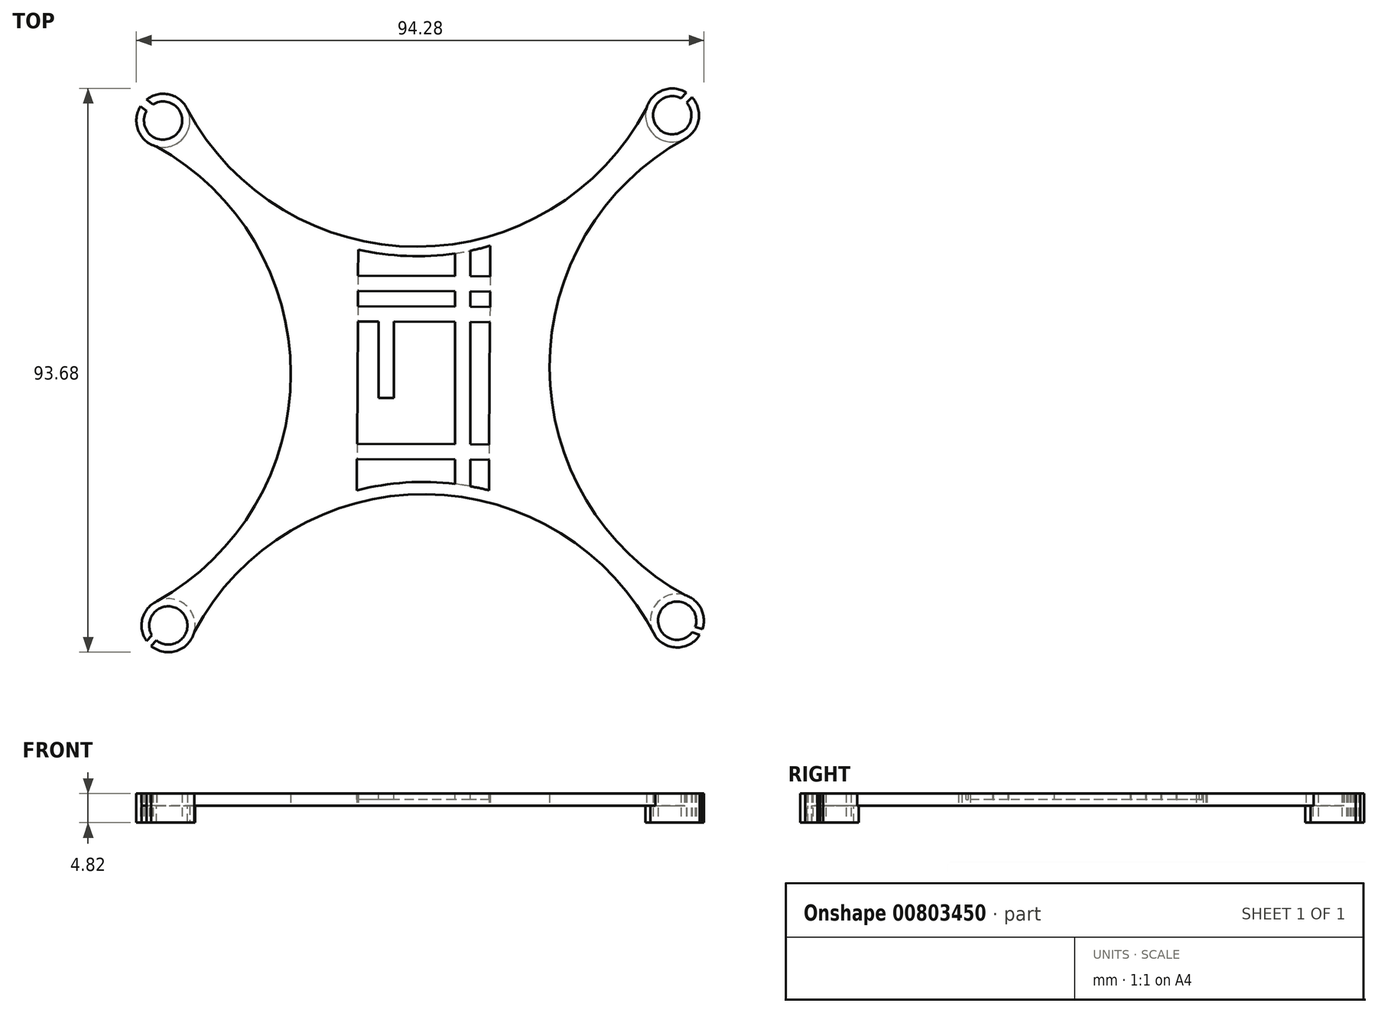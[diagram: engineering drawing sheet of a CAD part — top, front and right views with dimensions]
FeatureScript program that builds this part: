
annotation { "Feature Type Name" : "Feature", "Feature Type Description" : "" }
export const myFeature = defineFeature(function(context is Context, id is Id, definition is map)
    precondition{}
    {
        {
            var Q0;
            Q0=qCreatedBy(makeId("Top.planeOp"),FACE);
            var sketch = newSketch(context, id + "F0", { "sketchPlane" : qUnion([Q0])});
            skArc(sketch, "E0", {"start": v(2.55, 81.04) * mm, "mid": v(3.15, 81.98) * mm, "end": v(3.5, 83.03) * mm});
            skArc(sketch, "E1", {"start": v(3.18, 85.76) * mm, "mid": v(41.34, 62.94) * mm, "end": v(79.42, 85.92) * mm});
            skArc(sketch, "E2", {"start": v(-1.89, 4.02) * mm, "mid": v(20.35, 41.83) * mm, "end": v(-1.97, 79.6) * mm});
            skArc(sketch, "E3", {"start": v(80.92, 3.4) * mm, "mid": v(80.5, 2.69) * mm, "end": v(80.22, 1.92) * mm});
            skArc(sketch, "E4", {"start": v(80.89, -1.76) * mm, "mid": v(42.83, 21.8) * mm, "end": v(4.32, -1.04) * mm});
            skArc(sketch, "E5", {"start": v(85.7, 80.8) * mm, "mid": v(63.32, 42.87) * mm, "end": v(85.88, 5.03) * mm});
            skArc(sketch, "E6", {"start": v(81.15, 81.15) * mm, "mid": v(81.88, 80.73) * mm, "end": v(82.67, 80.46) * mm});
            skArc(sketch, "E7", {"start": v(3.94, 1.18) * mm, "mid": v(2.62, 3.23) * mm, "end": v(0.42, 4.27) * mm});
            skArc(sketch, "E8", {"start": v(0.73, 3.1) * mm, "mid": v(-2.56, 1.87) * mm, "end": v(-2.73, -1.63) * mm});
            skArc(sketch, "E9", {"start": v(81.97, 2.67) * mm, "mid": v(82.61, -1.74) * mm, "end": v(87.03, -1.15) * mm});
            skArc(sketch, "E10", {"start": v(82.1, 82.04) * mm, "mid": v(86.16, 82.75) * mm, "end": v(86.11, 86.86) * mm});
            skArc(sketch, "E11", {"start": v(1.5, 81.77) * mm, "mid": v(1.56, 85.95) * mm, "end": v(-2.56, 86.58) * mm});
            skArc(sketch, "E12", {"start": v(0.42, 4.27) * mm, "mid": v(22.13, 41.92) * mm, "end": v(0.7, 79.73) * mm});
            skArc(sketch, "E13", {"start": v(3.5, 83.03) * mm, "mid": v(41.63, 61.36) * mm, "end": v(79.42, 83.63) * mm});
            skArc(sketch, "E14", {"start": v(82.61, 80.55) * mm, "mid": v(61.39, 42.55) * mm, "end": v(83.44, 5.02) * mm});
            skArc(sketch, "E15", {"start": v(80.22, 1.92) * mm, "mid": v(41.87, 23.84) * mm, "end": v(3.94, 1.18) * mm});
            skArc(sketch, "E16.trimOffspring", {"start": v(79.42, 83.63) * mm, "mid": v(79.74, 82.8) * mm, "end": v(80.21, 82.04) * mm});
            skArc(sketch, "E17.trimOffspring", {"start": v(85.7, 80.8) * mm, "mid": v(88.09, 83.98) * mm, "end": v(86.99, 87.79) * mm});
            skLineSegment(sketch, "E18.left", {"start": v(31.55, 62.46) * mm, "end": v(31.32, 22.44) * mm});
            skLineSegment(sketch, "E18.right", {"start": v(53.5, 63.1) * mm, "end": v(53.27, 22.44) * mm});
            skLineSegment(sketch, "E19", {"start": v(-2.56, 86.58) * mm, "end": v(-3.62, 87.38) * mm});
            skLineSegment(sketch, "E20", {"start": v(-3.6, 85.5) * mm, "end": v(-4.61, 86.28) * mm});
            skArc(sketch, "E21.trimOffspring", {"start": v(-4.61, 86.28) * mm, "mid": v(-5, 82.26) * mm, "end": v(-1.97, 79.6) * mm});
            skArc(sketch, "E22.trimOffspring", {"start": v(-3.6, 85.5) * mm, "mid": v(-2.74, 81.34) * mm, "end": v(1.5, 81.77) * mm});
            skLineSegment(sketch, "E23", {"start": v(80.21, 82.04) * mm, "end": v(81.15, 81.15) * mm});
            skPoint(sketch, "E24.start.orphan", {"position": v(82.1, 82.04) * mm});
            skLineSegment(sketch, "E25", {"start": v(85.16, 87.6) * mm, "end": v(86.07, 88.55) * mm});
            skLineSegment(sketch, "E26", {"start": v(86.11, 86.86) * mm, "end": v(86.99, 87.79) * mm});
            skArc(sketch, "E27.trimOffspring", {"start": v(86.07, 88.55) * mm, "mid": v(82.08, 88.91) * mm, "end": v(79.42, 85.92) * mm});
            skArc(sketch, "E28.trimOffspring", {"start": v(85.16, 87.6) * mm, "mid": v(80.93, 86.31) * mm, "end": v(82.1, 82.04) * mm});
            skLineSegment(sketch, "E29", {"start": v(87.53, -0.22) * mm, "end": v(88.73, -0.65) * mm});
            skLineSegment(sketch, "E30", {"start": v(87.03, -1.15) * mm, "end": v(88.27, -1.6) * mm});
            skArc(sketch, "E31.trimOffspring", {"start": v(87.53, -0.22) * mm, "mid": v(85.99, 3.61) * mm, "end": v(81.97, 2.67) * mm});
            skArc(sketch, "E32.trimOffspring", {"start": v(88.73, -0.65) * mm, "mid": v(88.5, 2.8) * mm, "end": v(85.88, 5.03) * mm});
            skArc(sketch, "E33.trimOffspring", {"start": v(80.89, -1.76) * mm, "mid": v(84.62, -3.65) * mm, "end": v(88.27, -1.6) * mm});
            skArc(sketch, "E34.trimOffspring", {"start": v(83.49, 5.12) * mm, "mid": v(82.05, 4.49) * mm, "end": v(80.92, 3.4) * mm});
            skArc(sketch, "E35.trimOffspring", {"start": v(3.18, 85.76) * mm, "mid": v(0.17, 88.22) * mm, "end": v(-3.62, 87.38) * mm});
            skArc(sketch, "E36.trimOffspring", {"start": v(0.7, 79.73) * mm, "mid": v(1.7, 80.27) * mm, "end": v(2.55, 81.04) * mm});
            skArc(sketch, "E37.trimOffspring", {"start": v(-1.89, 4.02) * mm, "mid": v(-4.3, 1.13) * mm, "end": v(-3.63, -2.57) * mm});
            skLineSegment(sketch, "E38", {"start": v(-2.73, -1.63) * mm, "end": v(-3.63, -2.57) * mm});
            skLineSegment(sketch, "E39", {"start": v(-1.99, -2.48) * mm, "end": v(-2.87, -3.4) * mm});
            skArc(sketch, "E40.trimOffspring", {"start": v(-1.99, -2.48) * mm, "mid": v(2.85, -1.4) * mm, "end": v(0.73, 3.1) * mm});
            skArc(sketch, "E41.trimOffspring", {"start": v(-2.87, -3.4) * mm, "mid": v(1.39, -4.22) * mm, "end": v(4.32, -1.04) * mm});
            skSolve(sketch);
        }
        {
            var Q0;
            Q0 = qSketchRegion(id + "F0", true);
            var Q1;
            {var subQ1=sQuery(id+"F0.wireOp",EDGE,"E0");Q1=makeQuery(id+"F0.imprint","IMPRINT",FACE,{"disambiguationData":[TD([[makeQuery(id+"F0.imprint","IMPRINT",EDGE,{"derivedFrom":subQ1}),-1.0]])]});}
            var Q2;
            {var subQ10=sQuery(id+"F0.wireOp",EDGE,"E3");Q2=makeQuery(id+"F0.imprint","IMPRINT",FACE,{"disambiguationData":[TD([[makeQuery(id+"F0.imprint","IMPRINT",EDGE,{"derivedFrom":subQ10}),-1.0]])]});}
            extrude(context, id + "F1", {"entities" : qUnion([Q0, Q1, Q2]), "depth" : 2.03 * mm, "offsetDistance" : 25.4 * mm});
        }
        {
            var Q0;
            Q0=makeQuery(id+"F1.opExtrude","CAP_FACE",FACE,{"disambiguationData":[OSD([sQuery(id+"F0.wireOp",EDGE,"E1"),sQuery(id+"F0.wireOp",EDGE,"E2"),sQuery(id+"F0.wireOp",EDGE,"E4"),sQuery(id+"F0.wireOp",EDGE,"E5"),sQuery(id+"F0.wireOp",EDGE,"E8"),sQuery(id+"F0.wireOp",EDGE,"E9"),sQuery(id+"F0.wireOp",EDGE,"E10"),sQuery(id+"F0.wireOp",EDGE,"E11"),sQuery(id+"F0.wireOp",EDGE,"E13"),sQuery(id+"F0.wireOp",EDGE,"E15"),sQuery(id+"F0.wireOp",EDGE,"E17.trimOffspring"),sQuery(id+"F0.wireOp",EDGE,"E18.left"),sQuery(id+"F0.wireOp",EDGE,"E18.right"),sQuery(id+"F0.wireOp",EDGE,"eqaQngmX-uh6a-GMs2-6D1B-opZ38BFLEcCy"),sQuery(id+"F0.wireOp",EDGE,"E19"),sQuery(id+"F0.wireOp",EDGE,"E20"),sQuery(id+"F0.wireOp",EDGE,"E21.trimOffspring"),sQuery(id+"F0.wireOp",EDGE,"E22.trimOffspring"),sQuery(id+"F0.wireOp",EDGE,"Ete763jC-c4cK-E3Gr-KiQm-Rstjx0JgwXMj"),sQuery(id+"F0.wireOp",EDGE,"E25"),sQuery(id+"F0.wireOp",EDGE,"E26"),sQuery(id+"F0.wireOp",EDGE,"E27.trimOffspring"),sQuery(id+"F0.wireOp",EDGE,"E28.trimOffspring"),sQuery(id+"F0.wireOp",EDGE,"EZOsTXFy-vUSw-T1vB-YE65-mSjFuZfcAhLY"),sQuery(id+"F0.wireOp",EDGE,"E29"),sQuery(id+"F0.wireOp",EDGE,"E30"),sQuery(id+"F0.wireOp",EDGE,"E31.trimOffspring"),sQuery(id+"F0.wireOp",EDGE,"E32.trimOffspring"),sQuery(id+"F0.wireOp",EDGE,"E33.trimOffspring"),sQuery(id+"F0.wireOp",EDGE,"E35.trimOffspring"),sQuery(id+"F0.wireOp",EDGE,"E37.trimOffspring"),sQuery(id+"F0.wireOp",EDGE,"E38"),sQuery(id+"F0.wireOp",EDGE,"E39"),sQuery(id+"F0.wireOp",EDGE,"E40.trimOffspring"),sQuery(id+"F0.wireOp",EDGE,"E41.trimOffspring"),sQuery(id+"F0.wireOp",EDGE,"VMqzf1bx-NL3M-evuV-t4QN-v2y7nDxeiisL")])],"isStart":false});
            var sketch = newSketch(context, id + "F2", { "sketchPlane" : qUnion([Q0])});
            skPoint(sketch, "E42.oppositeSnap0", {"position": v(42.57, 61.38) * mm});
            skLineSegment(sketch, "E42.right", {"start": v(42.5, 61.38) * mm, "end": v(42.57, 23.84) * mm});
            skLineSegment(sketch, "E43", {"start": v(53.39, 42.77) * mm, "end": v(31.44, 42.9) * mm});
            skLineSegment(sketch, "E44", {"start": v(53.4, 45.31) * mm, "end": v(31.45, 45.44) * mm});
            skLineSegment(sketch, "E45", {"start": v(53.42, 47.85) * mm, "end": v(31.47, 47.98) * mm});
            skLineSegment(sketch, "E46", {"start": v(53.43, 50.4) * mm, "end": v(31.48, 50.52) * mm});
            skLineSegment(sketch, "E47", {"start": v(53.45, 52.93) * mm, "end": v(31.5, 53.06) * mm});
            skLineSegment(sketch, "E48", {"start": v(53.46, 55.47) * mm, "end": v(31.51, 55.6) * mm});
            skLineSegment(sketch, "E49", {"start": v(53.48, 58.01) * mm, "end": v(31.53, 58.14) * mm});
            skLineSegment(sketch, "E50", {"start": v(53.37, 40.23) * mm, "end": v(31.42, 40.36) * mm});
            skLineSegment(sketch, "E51", {"start": v(53.36, 37.7) * mm, "end": v(31.4, 37.82) * mm});
            skLineSegment(sketch, "E52", {"start": v(53.34, 35.15) * mm, "end": v(31.4, 35.28) * mm});
            skLineSegment(sketch, "E53", {"start": v(53.33, 32.61) * mm, "end": v(31.38, 32.74) * mm});
            skLineSegment(sketch, "E54", {"start": v(53.31, 30.07) * mm, "end": v(31.36, 30.2) * mm});
            skLineSegment(sketch, "E55", {"start": v(53.3, 27.53) * mm, "end": v(31.35, 27.66) * mm});
            skLineSegment(sketch, "E56", {"start": v(45.04, 61.52) * mm, "end": v(45.11, 23.75) * mm});
            skLineSegment(sketch, "E57", {"start": v(47.65, 61.83) * mm, "end": v(47.65, 23.5) * mm});
            skLineSegment(sketch, "E58", {"start": v(50.2, 62.28) * mm, "end": v(50.2, 23.12) * mm});
            skLineSegment(sketch, "E59", {"start": v(37.5, 61.53) * mm, "end": v(37.5, 23.57) * mm});
            skLineSegment(sketch, "E60", {"start": v(34.95, 61.82) * mm, "end": v(34.95, 23.22) * mm});
            skLineSegment(sketch, "E61", {"start": v(40.03, 61.38) * mm, "end": v(40.03, 23.78) * mm});
            skSolve(sketch);
        }
        {
            var Q0;
            Q0=makeQuery(id+"F1.opExtrude","CAP_FACE",FACE,{"disambiguationData":[OSD([sQuery(id+"F0.wireOp",EDGE,"E1"),sQuery(id+"F0.wireOp",EDGE,"E2"),sQuery(id+"F0.wireOp",EDGE,"E4"),sQuery(id+"F0.wireOp",EDGE,"E5"),sQuery(id+"F0.wireOp",EDGE,"E8"),sQuery(id+"F0.wireOp",EDGE,"E9"),sQuery(id+"F0.wireOp",EDGE,"E10"),sQuery(id+"F0.wireOp",EDGE,"E11"),sQuery(id+"F0.wireOp",EDGE,"E13"),sQuery(id+"F0.wireOp",EDGE,"E15"),sQuery(id+"F0.wireOp",EDGE,"E17.trimOffspring"),sQuery(id+"F0.wireOp",EDGE,"E18.left"),sQuery(id+"F0.wireOp",EDGE,"E18.right"),sQuery(id+"F0.wireOp",EDGE,"eqaQngmX-uh6a-GMs2-6D1B-opZ38BFLEcCy"),sQuery(id+"F0.wireOp",EDGE,"E19"),sQuery(id+"F0.wireOp",EDGE,"E20"),sQuery(id+"F0.wireOp",EDGE,"E21.trimOffspring"),sQuery(id+"F0.wireOp",EDGE,"E22.trimOffspring"),sQuery(id+"F0.wireOp",EDGE,"Ete763jC-c4cK-E3Gr-KiQm-Rstjx0JgwXMj"),sQuery(id+"F0.wireOp",EDGE,"E25"),sQuery(id+"F0.wireOp",EDGE,"E26"),sQuery(id+"F0.wireOp",EDGE,"E27.trimOffspring"),sQuery(id+"F0.wireOp",EDGE,"E28.trimOffspring"),sQuery(id+"F0.wireOp",EDGE,"EZOsTXFy-vUSw-T1vB-YE65-mSjFuZfcAhLY"),sQuery(id+"F0.wireOp",EDGE,"E29"),sQuery(id+"F0.wireOp",EDGE,"E30"),sQuery(id+"F0.wireOp",EDGE,"E31.trimOffspring"),sQuery(id+"F0.wireOp",EDGE,"E32.trimOffspring"),sQuery(id+"F0.wireOp",EDGE,"E33.trimOffspring"),sQuery(id+"F0.wireOp",EDGE,"E35.trimOffspring"),sQuery(id+"F0.wireOp",EDGE,"E37.trimOffspring"),sQuery(id+"F0.wireOp",EDGE,"E38"),sQuery(id+"F0.wireOp",EDGE,"E39"),sQuery(id+"F0.wireOp",EDGE,"E40.trimOffspring"),sQuery(id+"F0.wireOp",EDGE,"E41.trimOffspring"),sQuery(id+"F0.wireOp",EDGE,"VMqzf1bx-NL3M-evuV-t4QN-v2y7nDxeiisL")])],"isStart":true});
            var sketch = newSketch(context, id + "F3", { "sketchPlane" : qUnion([Q0])});
            skPoint(sketch, "E62.center.orphan", {"position": v(84.52, -0.8) * mm});
            skPoint(sketch, "E63.center.orphan", {"position": v(-0.86, -83.9) * mm});
            skPoint(sketch, "E64.center.orphan", {"position": v(83.72, -84.78) * mm});
            skArc(sketch, "E65", {"start": v(86.11, -86.86) * mm, "mid": v(81.76, -82.28) * mm, "end": v(85.16, -87.6) * mm});
            skArc(sketch, "E66", {"start": v(86.99, -87.79) * mm, "mid": v(80.88, -81.36) * mm, "end": v(86.07, -88.55) * mm});
            skLineSegment(sketch, "E67", {"start": v(86.11, -86.86) * mm, "end": v(86.99, -87.79) * mm});
            skLineSegment(sketch, "E68", {"start": v(85.16, -87.6) * mm, "end": v(86.07, -88.55) * mm});
            skArc(sketch, "E69", {"start": v(-2.72, 1.63) * mm, "mid": v(2.4, -2.08) * mm, "end": v(-1.99, 2.48) * mm});
            skLineSegment(sketch, "E70", {"start": v(-2.73, 1.63) * mm, "end": v(-3.63, 2.57) * mm});
            skLineSegment(sketch, "E71", {"start": v(-1.99, 2.48) * mm, "end": v(-2.87, 3.4) * mm});
            skArc(sketch, "E72", {"start": v(-2.56, -86.58) * mm, "mid": v(1.42, -81.69) * mm, "end": v(-3.6, -85.5) * mm});
            skArc(sketch, "E73", {"start": v(-3.62, -87.38) * mm, "mid": v(2.44, -80.92) * mm, "end": v(-4.61, -86.28) * mm});
            skLineSegment(sketch, "E74", {"start": v(-4.61, -86.28) * mm, "end": v(-3.6, -85.5) * mm});
            skLineSegment(sketch, "E75", {"start": v(-2.56, -86.58) * mm, "end": v(-3.62, -87.38) * mm});
            skArc(sketch, "E76", {"start": v(87.03, 1.15) * mm, "mid": v(81.73, -2.3) * mm, "end": v(87.53, 0.22) * mm});
            skArc(sketch, "E77", {"start": v(88.27, 1.6) * mm, "mid": v(80.52, -2.72) * mm, "end": v(88.73, 0.65) * mm});
            skLineSegment(sketch, "E78", {"start": v(88.73, 0.65) * mm, "end": v(87.53, 0.22) * mm});
            skLineSegment(sketch, "E79", {"start": v(88.27, 1.6) * mm, "end": v(87.03, 1.15) * mm});
            skArc(sketch, "E80", {"start": v(-3.63, 2.57) * mm, "mid": v(3.28, -3) * mm, "end": v(-2.87, 3.4) * mm});
            skSolve(sketch);
        }
        {
            var Q0;
            Q0 = qSketchRegion(id + "F3", true);
            var Q1;
            {var subQ2=sQuery(id+"F3.wireOp",EDGE,"E70");Q1=makeQuery(id+"F3.imprint","IMPRINT",FACE,{"disambiguationData":[TD([[makeQuery(id+"F3.imprint","IMPRINT",EDGE,{"derivedFrom":subQ2}),1.0]])]});}
            extrude(context, id + "F4", {"entities" : qUnion([Q0, Q1]), "operationType" : NewBodyOperationType.ADD, "depth" : 2.8 * mm, "offsetDistance" : 25.4 * mm});
        }
        {
            var Q0;
            {var subQ0=sQuery(id+"F2.wireOp",EDGE,"E49");var subQ1=sQuery(id+"F2.wireOp",EDGE,"E42.right");var subQ2=makeQuery(id+"F2.imprint","INTERSECT",VERTEX,{"derivedFrom":[subQ1,subQ0]});Q0=makeQuery(id+"F2.imprint","IMPRINT",FACE,{"disambiguationData":[TD([[makeQuery(id+"F2.imprint","IMPRINT",EDGE,{"disambiguationData":[TD([[subQ2,-1.0]])],"derivedFrom":subQ1}),1.0]])]});}
            var Q1;
            {var subQ0=sQuery(id+"F2.wireOp",EDGE,"E49");var subQ1=sQuery(id+"F2.wireOp",EDGE,"E42.right");var subQ2=makeQuery(id+"F2.imprint","INTERSECT",VERTEX,{"derivedFrom":[subQ1,subQ0]});Q1=makeQuery(id+"F2.imprint","IMPRINT",FACE,{"disambiguationData":[TD([[makeQuery(id+"F2.imprint","IMPRINT",EDGE,{"disambiguationData":[TD([[subQ2,-1.0]])],"derivedFrom":subQ1}),-1.0]])]});}
            var Q2;
            {var subQ0=sQuery(id+"F2.wireOp",EDGE,"E54");var subQ1=sQuery(id+"F2.wireOp",EDGE,"E42.right");var subQ2=makeQuery(id+"F2.imprint","INTERSECT",VERTEX,{"derivedFrom":[subQ1,subQ0]});Q2=makeQuery(id+"F2.imprint","IMPRINT",FACE,{"disambiguationData":[TD([[makeQuery(id+"F2.imprint","IMPRINT",EDGE,{"disambiguationData":[TD([[subQ2,-1.0]])],"derivedFrom":subQ1}),1.0]])]});}
            var Q3;
            {var subQ0=sQuery(id+"F2.wireOp",EDGE,"E54");var subQ1=sQuery(id+"F2.wireOp",EDGE,"E42.right");var subQ2=makeQuery(id+"F2.imprint","INTERSECT",VERTEX,{"derivedFrom":[subQ1,subQ0]});Q3=makeQuery(id+"F2.imprint","IMPRINT",FACE,{"disambiguationData":[TD([[makeQuery(id+"F2.imprint","IMPRINT",EDGE,{"disambiguationData":[TD([[subQ2,-1.0]])],"derivedFrom":subQ1}),-1.0]])]});}
            var Q4;
            {var subQ0=sQuery(id+"F2.wireOp",EDGE,"E58");var subQ1=sQuery(id+"F2.wireOp",EDGE,"E43");var subQ2=makeQuery(id+"F2.imprint","INTERSECT",VERTEX,{"derivedFrom":[subQ1,subQ0]});Q4=makeQuery(id+"F2.imprint","IMPRINT",FACE,{"disambiguationData":[TD([[makeQuery(id+"F2.imprint","IMPRINT",EDGE,{"disambiguationData":[TD([[subQ2,-1.0]])],"derivedFrom":subQ1}),-1.0]])]});}
            var Q5;
            {var subQ0=sQuery(id+"F2.wireOp",EDGE,"E58");var subQ1=sQuery(id+"F2.wireOp",EDGE,"E43");var subQ2=makeQuery(id+"F2.imprint","INTERSECT",VERTEX,{"derivedFrom":[subQ1,subQ0]});Q5=makeQuery(id+"F2.imprint","IMPRINT",FACE,{"disambiguationData":[TD([[makeQuery(id+"F2.imprint","IMPRINT",EDGE,{"disambiguationData":[TD([[subQ2,-1.0]])],"derivedFrom":subQ1}),1.0]])]});}
            var Q6;
            {var subQ0=sQuery(id+"F2.wireOp",EDGE,"E58");var subQ1=sQuery(id+"F2.wireOp",EDGE,"E44");var subQ2=makeQuery(id+"F2.imprint","INTERSECT",VERTEX,{"derivedFrom":[subQ1,subQ0]});Q6=makeQuery(id+"F2.imprint","IMPRINT",FACE,{"disambiguationData":[TD([[makeQuery(id+"F2.imprint","IMPRINT",EDGE,{"disambiguationData":[TD([[subQ2,-1.0]])],"derivedFrom":subQ1}),-1.0]])]});}
            var Q7;
            {var subQ0=sQuery(id+"F2.wireOp",EDGE,"E58");var subQ1=sQuery(id+"F2.wireOp",EDGE,"E45");var subQ2=makeQuery(id+"F2.imprint","INTERSECT",VERTEX,{"derivedFrom":[subQ1,subQ0]});Q7=makeQuery(id+"F2.imprint","IMPRINT",FACE,{"disambiguationData":[TD([[makeQuery(id+"F2.imprint","IMPRINT",EDGE,{"disambiguationData":[TD([[subQ2,-1.0]])],"derivedFrom":subQ1}),-1.0]])]});}
            var Q8;
            {var subQ0=sQuery(id+"F2.wireOp",EDGE,"E58");var subQ1=sQuery(id+"F2.wireOp",EDGE,"E46");var subQ2=makeQuery(id+"F2.imprint","INTERSECT",VERTEX,{"derivedFrom":[subQ1,subQ0]});Q8=makeQuery(id+"F2.imprint","IMPRINT",FACE,{"disambiguationData":[TD([[makeQuery(id+"F2.imprint","IMPRINT",EDGE,{"disambiguationData":[TD([[subQ2,-1.0]])],"derivedFrom":subQ1}),-1.0]])]});}
            var Q9;
            {var subQ0=sQuery(id+"F2.wireOp",EDGE,"E59");var subQ1=sQuery(id+"F2.wireOp",EDGE,"E46");var subQ2=makeQuery(id+"F2.imprint","INTERSECT",VERTEX,{"derivedFrom":[subQ1,subQ0]});Q9=makeQuery(id+"F2.imprint","IMPRINT",FACE,{"disambiguationData":[TD([[makeQuery(id+"F2.imprint","IMPRINT",EDGE,{"disambiguationData":[TD([[subQ2,-1.0]])],"derivedFrom":subQ1}),-1.0]])]});}
            var Q10;
            {var subQ0=sQuery(id+"F2.wireOp",EDGE,"E58");var subQ1=sQuery(id+"F2.wireOp",EDGE,"E48");var subQ2=makeQuery(id+"F2.imprint","INTERSECT",VERTEX,{"derivedFrom":[subQ1,subQ0]});Q10=makeQuery(id+"F2.imprint","IMPRINT",FACE,{"disambiguationData":[TD([[makeQuery(id+"F2.imprint","IMPRINT",EDGE,{"disambiguationData":[TD([[subQ2,-1.0]])],"derivedFrom":subQ1}),-1.0]])]});}
            var Q11;
            {var subQ0=sQuery(id+"F2.wireOp",EDGE,"E57");var subQ1=sQuery(id+"F2.wireOp",EDGE,"E48");var subQ2=makeQuery(id+"F2.imprint","INTERSECT",VERTEX,{"derivedFrom":[subQ1,subQ0]});Q11=makeQuery(id+"F2.imprint","IMPRINT",FACE,{"disambiguationData":[TD([[makeQuery(id+"F2.imprint","IMPRINT",EDGE,{"disambiguationData":[TD([[subQ2,-1.0]])],"derivedFrom":subQ1}),-1.0]])]});}
            var Q12;
            {var subQ0=sQuery(id+"F2.wireOp",EDGE,"E61");var subQ1=sQuery(id+"F2.wireOp",EDGE,"E48");var subQ2=makeQuery(id+"F2.imprint","INTERSECT",VERTEX,{"derivedFrom":[subQ1,subQ0]});Q12=makeQuery(id+"F2.imprint","IMPRINT",FACE,{"disambiguationData":[TD([[makeQuery(id+"F2.imprint","IMPRINT",EDGE,{"disambiguationData":[TD([[subQ2,-1.0]])],"derivedFrom":subQ1}),-1.0]])]});}
            var Q13;
            {var subQ0=sQuery(id+"F2.wireOp",EDGE,"E59");var subQ1=sQuery(id+"F2.wireOp",EDGE,"E48");var subQ2=makeQuery(id+"F2.imprint","INTERSECT",VERTEX,{"derivedFrom":[subQ1,subQ0]});Q13=makeQuery(id+"F2.imprint","IMPRINT",FACE,{"disambiguationData":[TD([[makeQuery(id+"F2.imprint","IMPRINT",EDGE,{"disambiguationData":[TD([[subQ2,-1.0]])],"derivedFrom":subQ1}),-1.0]])]});}
            var Q14;
            {var subQ0=sQuery(id+"F2.wireOp",EDGE,"E58");var subQ1=sQuery(id+"F2.wireOp",EDGE,"E50");var subQ2=makeQuery(id+"F2.imprint","INTERSECT",VERTEX,{"derivedFrom":[subQ1,subQ0]});Q14=makeQuery(id+"F2.imprint","IMPRINT",FACE,{"disambiguationData":[TD([[makeQuery(id+"F2.imprint","IMPRINT",EDGE,{"disambiguationData":[TD([[subQ2,-1.0]])],"derivedFrom":subQ1}),1.0]])]});}
            var Q15;
            {var subQ0=sQuery(id+"F2.wireOp",EDGE,"E58");var subQ1=sQuery(id+"F2.wireOp",EDGE,"E51");var subQ2=makeQuery(id+"F2.imprint","INTERSECT",VERTEX,{"derivedFrom":[subQ1,subQ0]});Q15=makeQuery(id+"F2.imprint","IMPRINT",FACE,{"disambiguationData":[TD([[makeQuery(id+"F2.imprint","IMPRINT",EDGE,{"disambiguationData":[TD([[subQ2,-1.0]])],"derivedFrom":subQ1}),1.0]])]});}
            var Q16;
            {var subQ0=sQuery(id+"F2.wireOp",EDGE,"E58");var subQ1=sQuery(id+"F2.wireOp",EDGE,"E52");var subQ2=makeQuery(id+"F2.imprint","INTERSECT",VERTEX,{"derivedFrom":[subQ1,subQ0]});Q16=makeQuery(id+"F2.imprint","IMPRINT",FACE,{"disambiguationData":[TD([[makeQuery(id+"F2.imprint","IMPRINT",EDGE,{"disambiguationData":[TD([[subQ2,-1.0]])],"derivedFrom":subQ1}),1.0]])]});}
            var Q17;
            {var subQ0=sQuery(id+"F2.wireOp",EDGE,"E58");var subQ1=sQuery(id+"F2.wireOp",EDGE,"E53");var subQ2=makeQuery(id+"F2.imprint","INTERSECT",VERTEX,{"derivedFrom":[subQ1,subQ0]});Q17=makeQuery(id+"F2.imprint","IMPRINT",FACE,{"disambiguationData":[TD([[makeQuery(id+"F2.imprint","IMPRINT",EDGE,{"disambiguationData":[TD([[subQ2,-1.0]])],"derivedFrom":subQ1}),1.0]])]});}
            var Q18;
            {var subQ0=sQuery(id+"F2.wireOp",EDGE,"E58");var subQ1=sQuery(id+"F2.wireOp",EDGE,"E54");var subQ2=makeQuery(id+"F2.imprint","INTERSECT",VERTEX,{"derivedFrom":[subQ1,subQ0]});Q18=makeQuery(id+"F2.imprint","IMPRINT",FACE,{"disambiguationData":[TD([[makeQuery(id+"F2.imprint","IMPRINT",EDGE,{"disambiguationData":[TD([[subQ2,-1.0]])],"derivedFrom":subQ1}),1.0]])]});}
            var Q19;
            {var subQ0=sQuery(id+"F2.wireOp",EDGE,"E57");var subQ1=sQuery(id+"F2.wireOp",EDGE,"E54");var subQ2=makeQuery(id+"F2.imprint","INTERSECT",VERTEX,{"derivedFrom":[subQ1,subQ0]});Q19=makeQuery(id+"F2.imprint","IMPRINT",FACE,{"disambiguationData":[TD([[makeQuery(id+"F2.imprint","IMPRINT",EDGE,{"disambiguationData":[TD([[subQ2,-1.0]])],"derivedFrom":subQ1}),1.0]])]});}
            var Q20;
            {var subQ0=sQuery(id+"F2.wireOp",EDGE,"E61");var subQ1=sQuery(id+"F2.wireOp",EDGE,"E54");var subQ2=makeQuery(id+"F2.imprint","INTERSECT",VERTEX,{"derivedFrom":[subQ1,subQ0]});Q20=makeQuery(id+"F2.imprint","IMPRINT",FACE,{"disambiguationData":[TD([[makeQuery(id+"F2.imprint","IMPRINT",EDGE,{"disambiguationData":[TD([[subQ2,-1.0]])],"derivedFrom":subQ1}),1.0]])]});}
            var Q21;
            {var subQ0=sQuery(id+"F2.wireOp",EDGE,"E59");var subQ1=sQuery(id+"F2.wireOp",EDGE,"E54");var subQ2=makeQuery(id+"F2.imprint","INTERSECT",VERTEX,{"derivedFrom":[subQ1,subQ0]});Q21=makeQuery(id+"F2.imprint","IMPRINT",FACE,{"disambiguationData":[TD([[makeQuery(id+"F2.imprint","IMPRINT",EDGE,{"disambiguationData":[TD([[subQ2,-1.0]])],"derivedFrom":subQ1}),1.0]])]});}
            var Q22;
            {var subQ0=sQuery(id+"F2.wireOp",EDGE,"E54");var subQ1=makeQuery(id+"F1.opExtrude","CAP_EDGE",EDGE,{"disambiguationData":[OSD([sQuery(id+"F0.wireOp",EDGE,"E18.left")])],"isStart":false});var subQ2=makeQuery(id+"F2.imprint","INTERSECT",VERTEX,{"derivedFrom":[subQ1,subQ0]});Q22=makeQuery(id+"F2.imprint","IMPRINT",FACE,{"disambiguationData":[TD([[makeQuery(id+"F2.imprint","IMPRINT",EDGE,{"disambiguationData":[TD([[subQ2,1.0]])],"derivedFrom":subQ0}),1.0]])]});}
            var Q23;
            {var subQ0=sQuery(id+"F2.wireOp",EDGE,"E54");var subQ1=makeQuery(id+"F1.opExtrude","CAP_EDGE",EDGE,{"disambiguationData":[OSD([sQuery(id+"F0.wireOp",EDGE,"E18.right")])],"isStart":false});var subQ2=makeQuery(id+"F2.imprint","INTERSECT",VERTEX,{"derivedFrom":[subQ1,subQ0]});Q23=makeQuery(id+"F2.imprint","IMPRINT",FACE,{"disambiguationData":[TD([[makeQuery(id+"F2.imprint","IMPRINT",EDGE,{"disambiguationData":[TD([[subQ2,-1.0]])],"derivedFrom":subQ0}),1.0]])]});}
            var Q24;
            {var subQ0=sQuery(id+"F2.wireOp",EDGE,"E58");var subQ1=sQuery(id+"F2.wireOp",EDGE,"E49");var subQ2=makeQuery(id+"F2.imprint","INTERSECT",VERTEX,{"derivedFrom":[subQ1,subQ0]});Q24=makeQuery(id+"F2.imprint","IMPRINT",FACE,{"disambiguationData":[TD([[makeQuery(id+"F2.imprint","IMPRINT",EDGE,{"disambiguationData":[TD([[subQ2,-1.0]])],"derivedFrom":subQ1}),-1.0]])]});}
            var Q25;
            {var subQ0=sQuery(id+"F2.wireOp",EDGE,"E48");var subQ1=makeQuery(id+"F1.opExtrude","CAP_EDGE",EDGE,{"disambiguationData":[OSD([sQuery(id+"F0.wireOp",EDGE,"E18.right")])],"isStart":false});var subQ2=makeQuery(id+"F2.imprint","INTERSECT",VERTEX,{"derivedFrom":[subQ1,subQ0]});Q25=makeQuery(id+"F2.imprint","IMPRINT",FACE,{"disambiguationData":[TD([[makeQuery(id+"F2.imprint","IMPRINT",EDGE,{"disambiguationData":[TD([[subQ2,-1.0]])],"derivedFrom":subQ0}),-1.0]])]});}
            var Q26;
            {var subQ0=sQuery(id+"F2.wireOp",EDGE,"E48");var subQ1=makeQuery(id+"F1.opExtrude","CAP_EDGE",EDGE,{"disambiguationData":[OSD([sQuery(id+"F0.wireOp",EDGE,"E18.left")])],"isStart":false});var subQ2=makeQuery(id+"F2.imprint","INTERSECT",VERTEX,{"derivedFrom":[subQ1,subQ0]});Q26=makeQuery(id+"F2.imprint","IMPRINT",FACE,{"disambiguationData":[TD([[makeQuery(id+"F2.imprint","IMPRINT",EDGE,{"disambiguationData":[TD([[subQ2,1.0]])],"derivedFrom":subQ0}),-1.0]])]});}
            var Q27;
            {var subQ0=sQuery(id+"F2.wireOp",EDGE,"E46");var subQ1=makeQuery(id+"F1.opExtrude","CAP_EDGE",EDGE,{"disambiguationData":[OSD([sQuery(id+"F0.wireOp",EDGE,"E18.right")])],"isStart":false});var subQ2=makeQuery(id+"F2.imprint","INTERSECT",VERTEX,{"derivedFrom":[subQ1,subQ0]});Q27=makeQuery(id+"F2.imprint","IMPRINT",FACE,{"disambiguationData":[TD([[makeQuery(id+"F2.imprint","IMPRINT",EDGE,{"disambiguationData":[TD([[subQ2,-1.0]])],"derivedFrom":subQ0}),-1.0]])]});}
            var Q28;
            {var subQ0=sQuery(id+"F2.wireOp",EDGE,"E57");var subQ1=sQuery(id+"F2.wireOp",EDGE,"E46");var subQ2=makeQuery(id+"F2.imprint","INTERSECT",VERTEX,{"derivedFrom":[subQ1,subQ0]});Q28=makeQuery(id+"F2.imprint","IMPRINT",FACE,{"disambiguationData":[TD([[makeQuery(id+"F2.imprint","IMPRINT",EDGE,{"disambiguationData":[TD([[subQ2,-1.0]])],"derivedFrom":subQ1}),-1.0]])]});}
            var Q29;
            {var subQ0=sQuery(id+"F2.wireOp",EDGE,"E46");var subQ1=makeQuery(id+"F1.opExtrude","CAP_EDGE",EDGE,{"disambiguationData":[OSD([sQuery(id+"F0.wireOp",EDGE,"E18.left")])],"isStart":false});var subQ2=makeQuery(id+"F2.imprint","INTERSECT",VERTEX,{"derivedFrom":[subQ1,subQ0]});Q29=makeQuery(id+"F2.imprint","IMPRINT",FACE,{"disambiguationData":[TD([[makeQuery(id+"F2.imprint","IMPRINT",EDGE,{"disambiguationData":[TD([[subQ2,1.0]])],"derivedFrom":subQ0}),-1.0]])]});}
            var Q30;
            {var subQ0=sQuery(id+"F2.wireOp",EDGE,"E58");var subQ1=sQuery(id+"F2.wireOp",EDGE,"E55");var subQ2=makeQuery(id+"F2.imprint","INTERSECT",VERTEX,{"derivedFrom":[subQ1,subQ0]});Q30=makeQuery(id+"F2.imprint","IMPRINT",FACE,{"disambiguationData":[TD([[makeQuery(id+"F2.imprint","IMPRINT",EDGE,{"disambiguationData":[TD([[subQ2,-1.0]])],"derivedFrom":subQ1}),1.0]])]});}
            var Q31;
            {var subQ0=sQuery(id+"F2.wireOp",EDGE,"E47");var subQ1=sQuery(id+"F2.wireOp",EDGE,"E42.right");var subQ2=makeQuery(id+"F2.imprint","INTERSECT",VERTEX,{"derivedFrom":[subQ1,subQ0]});Q31=makeQuery(id+"F2.imprint","IMPRINT",FACE,{"disambiguationData":[TD([[makeQuery(id+"F2.imprint","IMPRINT",EDGE,{"disambiguationData":[TD([[subQ2,-1.0]])],"derivedFrom":subQ1}),1.0]])]});}
            var Q32;
            {var subQ0=sQuery(id+"F2.wireOp",EDGE,"E61");var subQ1=sQuery(id+"F2.wireOp",EDGE,"E46");var subQ2=makeQuery(id+"F2.imprint","INTERSECT",VERTEX,{"derivedFrom":[subQ1,subQ0]});Q32=makeQuery(id+"F2.imprint","IMPRINT",FACE,{"disambiguationData":[TD([[makeQuery(id+"F2.imprint","IMPRINT",EDGE,{"disambiguationData":[TD([[subQ2,-1.0]])],"derivedFrom":subQ1}),-1.0]])]});}
            var Q33;
            {var subQ0=sQuery(id+"F2.wireOp",EDGE,"E47");var subQ1=sQuery(id+"F2.wireOp",EDGE,"E42.right");var subQ2=makeQuery(id+"F2.imprint","INTERSECT",VERTEX,{"derivedFrom":[subQ1,subQ0]});Q33=makeQuery(id+"F2.imprint","IMPRINT",FACE,{"disambiguationData":[TD([[makeQuery(id+"F2.imprint","IMPRINT",EDGE,{"disambiguationData":[TD([[subQ2,-1.0]])],"derivedFrom":subQ1}),-1.0]])]});}
            var Q34;
            {var subQ0=sQuery(id+"F2.wireOp",EDGE,"E58");var subQ1=sQuery(id+"F2.wireOp",EDGE,"E47");var subQ2=makeQuery(id+"F2.imprint","INTERSECT",VERTEX,{"derivedFrom":[subQ1,subQ0]});Q34=makeQuery(id+"F2.imprint","IMPRINT",FACE,{"disambiguationData":[TD([[makeQuery(id+"F2.imprint","IMPRINT",EDGE,{"disambiguationData":[TD([[subQ2,-1.0]])],"derivedFrom":subQ1}),-1.0]])]});}
            var Q35;
            {var subQ0=sQuery(id+"F2.wireOp",EDGE,"E59");var subQ1=sQuery(id+"F2.wireOp",EDGE,"E50");var subQ2=makeQuery(id+"F2.imprint","INTERSECT",VERTEX,{"derivedFrom":[subQ1,subQ0]});Q35=makeQuery(id+"F2.imprint","IMPRINT",FACE,{"disambiguationData":[TD([[makeQuery(id+"F2.imprint","IMPRINT",EDGE,{"disambiguationData":[TD([[subQ2,-1.0]])],"derivedFrom":subQ1}),1.0]])]});}
            var Q36;
            {var subQ0=sQuery(id+"F2.wireOp",EDGE,"E59");var subQ1=sQuery(id+"F2.wireOp",EDGE,"E43");var subQ2=makeQuery(id+"F2.imprint","INTERSECT",VERTEX,{"derivedFrom":[subQ1,subQ0]});Q36=makeQuery(id+"F2.imprint","IMPRINT",FACE,{"disambiguationData":[TD([[makeQuery(id+"F2.imprint","IMPRINT",EDGE,{"disambiguationData":[TD([[subQ2,-1.0]])],"derivedFrom":subQ1}),1.0]])]});}
            var Q37;
            {var subQ0=sQuery(id+"F2.wireOp",EDGE,"E59");var subQ1=sQuery(id+"F2.wireOp",EDGE,"E43");var subQ2=makeQuery(id+"F2.imprint","INTERSECT",VERTEX,{"derivedFrom":[subQ1,subQ0]});Q37=makeQuery(id+"F2.imprint","IMPRINT",FACE,{"disambiguationData":[TD([[makeQuery(id+"F2.imprint","IMPRINT",EDGE,{"disambiguationData":[TD([[subQ2,-1.0]])],"derivedFrom":subQ1}),-1.0]])]});}
            var Q38;
            {var subQ0=sQuery(id+"F2.wireOp",EDGE,"E59");var subQ1=sQuery(id+"F2.wireOp",EDGE,"E44");var subQ2=makeQuery(id+"F2.imprint","INTERSECT",VERTEX,{"derivedFrom":[subQ1,subQ0]});Q38=makeQuery(id+"F2.imprint","IMPRINT",FACE,{"disambiguationData":[TD([[makeQuery(id+"F2.imprint","IMPRINT",EDGE,{"disambiguationData":[TD([[subQ2,-1.0]])],"derivedFrom":subQ1}),-1.0]])]});}
            var Q39;
            {var subQ0=sQuery(id+"F2.wireOp",EDGE,"E59");var subQ1=sQuery(id+"F2.wireOp",EDGE,"E45");var subQ2=makeQuery(id+"F2.imprint","INTERSECT",VERTEX,{"derivedFrom":[subQ1,subQ0]});Q39=makeQuery(id+"F2.imprint","IMPRINT",FACE,{"disambiguationData":[TD([[makeQuery(id+"F2.imprint","IMPRINT",EDGE,{"disambiguationData":[TD([[subQ2,-1.0]])],"derivedFrom":subQ1}),-1.0]])]});}
            extrude(context, id + "F5", {"entities" : qUnion([Q0, Q1, Q2, Q3, Q4, Q5, Q6, Q7, Q8, Q9, Q10, Q11, Q12, Q13, Q14, Q15, Q16, Q17, Q18, Q19, Q20, Q21, Q22, Q23, Q24, Q25, Q26, Q27, Q28, Q29, Q30, Q31, Q32, Q33, Q34, Q35, Q36, Q37, Q38, Q39]), "operationType" : NewBodyOperationType.ADD, "oppositeDirection" : true, "depth" : 1.02 * mm, "offsetDistance" : 25.4 * mm});
        }
    });
